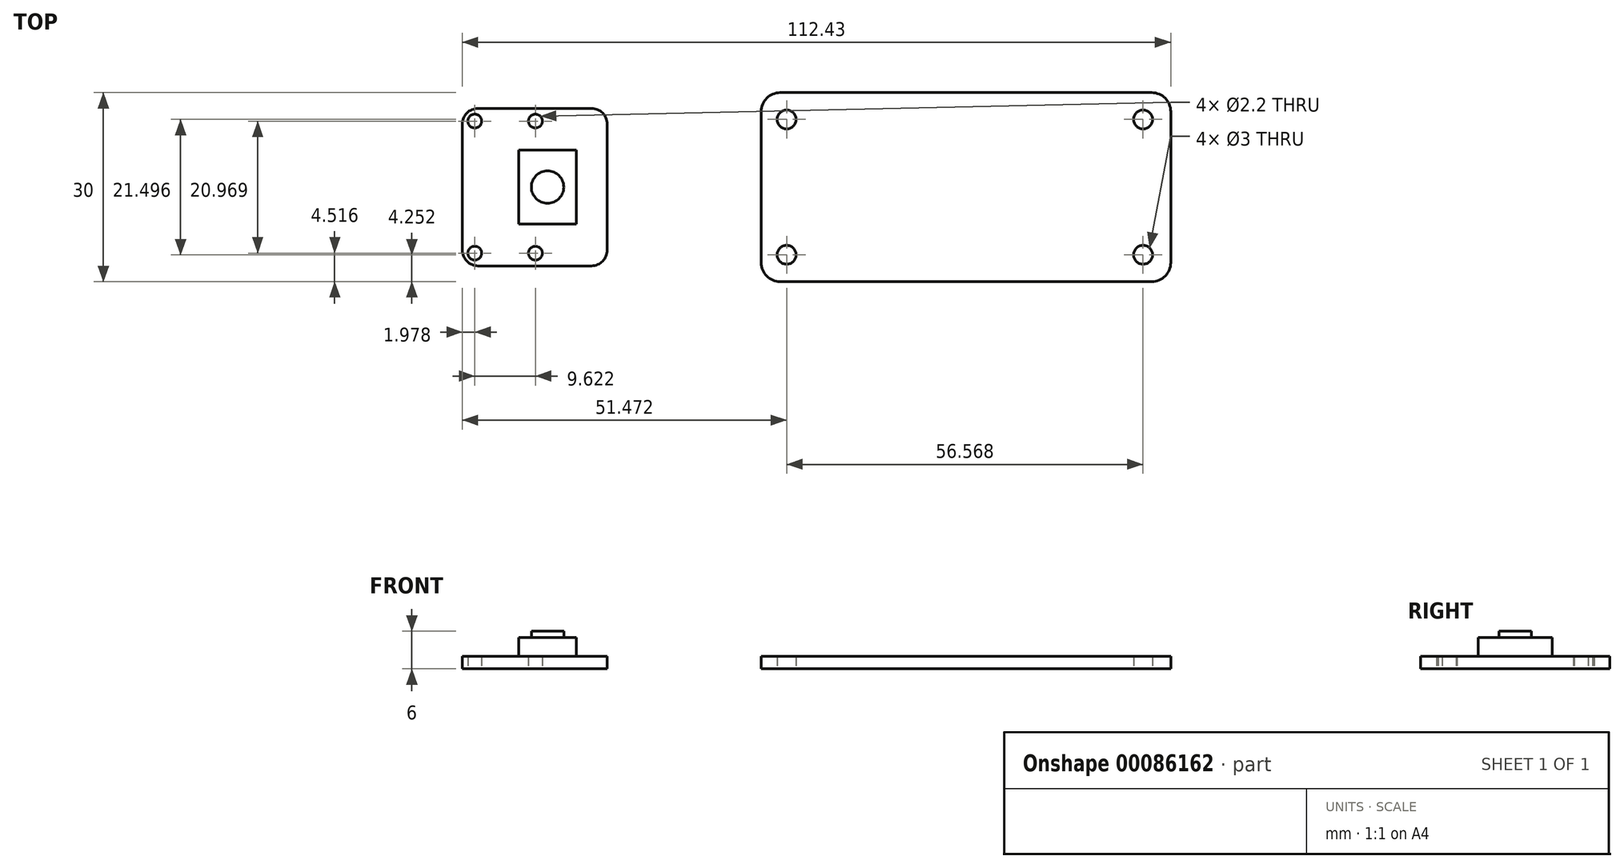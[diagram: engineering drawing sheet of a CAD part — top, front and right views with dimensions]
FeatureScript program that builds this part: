
annotation { "Feature Type Name" : "Feature", "Feature Type Description" : "" }
export const myFeature = defineFeature(function(context is Context, id is Id, definition is map)
    precondition{}
    {
        {
            var Q0;
            Q0=qCreatedBy(makeId("Top.planeOp"),FACE);
            var sketch = newSketch(context, id + "F0", { "sketchPlane" : qUnion([Q0])});
            skLineSegment(sketch, "E0.bottom", {"start": v(-29.5, 15) * mm, "end": v(29.5, 15) * mm});
            skLineSegment(sketch, "E0.top", {"start": v(-29.5, -15) * mm, "end": v(29.5, -15) * mm});
            skLineSegment(sketch, "E0.left", {"start": v(-32.5, 12) * mm, "end": v(-32.5, -12) * mm});
            skLineSegment(sketch, "E0.right", {"start": v(32.5, 12) * mm, "end": v(32.5, -12) * mm});
            skPoint(sketch, "E0.middle", {"position": v(0, 0) * mm});
            skLineSegment(sketch, "E1", {"start": v(-28.46, 35.85) * mm, "end": v(-28.46, -30.94) * mm, "construction": true});
            skLineSegment(sketch, "E2", {"start": v(28.1, 33.55) * mm, "end": v(28.1, -25.56) * mm, "construction": true});
            skLineSegment(sketch, "E3", {"start": v(-45.78, 10.75) * mm, "end": v(56.54, 10.75) * mm, "construction": true});
            skLineSegment(sketch, "E4", {"start": v(-43.57, -10.75) * mm, "end": v(50.84, -10.75) * mm, "construction": true});
            skCircle(sketch, "E5", {"center": v(-28.46, 10.75) * mm, "radius": 1.5 * mm});
            skCircle(sketch, "E6", {"center": v(28.1, 10.75) * mm, "radius": 1.5 * mm});
            skCircle(sketch, "E7", {"center": v(-28.46, -10.75) * mm, "radius": 1.5 * mm});
            skCircle(sketch, "E8", {"center": v(28.1, -10.75) * mm, "radius": 1.5 * mm});
            skPoint(sketch, "E9.visualSharp", {"position": v(-32.5, 15) * mm});
            skArc(sketch, "E9.filletArc", {"start": v(-29.5, 15) * mm, "mid": v(-31.62, 14.12) * mm, "end": v(-32.5, 12) * mm});
            skPoint(sketch, "E10.visualSharp", {"position": v(32.5, 15) * mm});
            skArc(sketch, "E10.filletArc", {"start": v(32.5, 12) * mm, "mid": v(31.62, 14.12) * mm, "end": v(29.5, 15) * mm});
            skPoint(sketch, "E11.visualSharp", {"position": v(32.5, -15) * mm});
            skArc(sketch, "E11.filletArc", {"start": v(29.5, -15) * mm, "mid": v(31.62, -14.12) * mm, "end": v(32.5, -12) * mm});
            skPoint(sketch, "E12.visualSharp", {"position": v(-32.5, -15) * mm});
            skArc(sketch, "E12.filletArc", {"start": v(-32.5, -12) * mm, "mid": v(-31.62, -14.12) * mm, "end": v(-29.5, -15) * mm});
            skSolve(sketch);
        }
        {
            var Q0;
            Q0=makeQuery(id+"F0.imprint","IMPRINT",FACE,{"disambiguationData":[TD([[makeQuery(id+"F0.imprint","IMPRINT",EDGE,{"derivedFrom":sQuery(id+"F0.wireOp",EDGE,"E0.bottom")}),-1.0]])]});
            extrude(context, id + "F1", {"entities" : qUnion([Q0]), "depth" : 2 * mm});
        }
        {
            var Q0;
            Q0=qCreatedBy(makeId("Top.planeOp"),FACE);
            var sketch = newSketch(context, id + "F2", { "sketchPlane" : qUnion([Q0])});
            skLineSegment(sketch, "E13.bottom", {"start": v(-77.43, 12.5) * mm, "end": v(-59.43, 12.5) * mm});
            skLineSegment(sketch, "E13.top", {"start": v(-77.43, -12.5) * mm, "end": v(-59.43, -12.5) * mm});
            skLineSegment(sketch, "E13.left", {"start": v(-79.93, 10) * mm, "end": v(-79.93, -10) * mm});
            skLineSegment(sketch, "E13.right", {"start": v(-56.93, 10) * mm, "end": v(-56.93, -10) * mm});
            skPoint(sketch, "E13.middle", {"position": v(-68.43, 0) * mm});
            skCircle(sketch, "E14", {"center": v(-77.95, 10.48) * mm, "radius": 1.1 * mm});
            skCircle(sketch, "E15", {"center": v(-68.33, 10.48) * mm, "radius": 1.1 * mm});
            skPoint(sketch, "E16.visualSharp", {"position": v(-79.93, 12.5) * mm});
            skArc(sketch, "E16.filletArc", {"start": v(-77.43, 12.5) * mm, "mid": v(-79.2, 11.77) * mm, "end": v(-79.93, 10) * mm});
            skPoint(sketch, "E17.visualSharp", {"position": v(-56.93, 12.5) * mm});
            skArc(sketch, "E17.filletArc", {"start": v(-56.93, 10) * mm, "mid": v(-57.66, 11.77) * mm, "end": v(-59.43, 12.5) * mm});
            skPoint(sketch, "E18.visualSharp", {"position": v(-56.93, -12.5) * mm});
            skArc(sketch, "E18.filletArc", {"start": v(-59.43, -12.5) * mm, "mid": v(-57.66, -11.77) * mm, "end": v(-56.93, -10) * mm});
            skPoint(sketch, "E19.visualSharp", {"position": v(-79.93, -12.5) * mm});
            skArc(sketch, "E19.filletArc", {"start": v(-79.93, -10) * mm, "mid": v(-79.2, -11.77) * mm, "end": v(-77.43, -12.5) * mm});
            skLineSegment(sketch, "E20", {"start": v(-51.58, 10.48) * mm, "end": v(-85.9, 10.48) * mm, "construction": true});
            skCircle(sketch, "E21.MirrorC", {"center": v(-68.33, -10.48) * mm, "radius": 1.1 * mm});
            skCircle(sketch, "E22.MirrorC", {"center": v(-77.95, -10.48) * mm, "radius": 1.1 * mm});
            skLineSegment(sketch, "E23.bottom", {"start": v(-71, 5.89) * mm, "end": v(-61.8, 5.89) * mm});
            skLineSegment(sketch, "E23.top", {"start": v(-71, -5.89) * mm, "end": v(-61.8, -5.89) * mm});
            skLineSegment(sketch, "E23.left", {"start": v(-71, 5.89) * mm, "end": v(-71, -5.89) * mm});
            skLineSegment(sketch, "E23.right", {"start": v(-61.8, 5.89) * mm, "end": v(-61.8, -5.89) * mm});
            skPoint(sketch, "E23.middle", {"position": v(-66.4, 0) * mm});
            skCircle(sketch, "E24", {"center": v(-66.4, 0) * mm, "radius": 2.57 * mm});
            skSolve(sketch);
        }
        {
            var Q0;
            Q0=makeQuery(id+"F2.imprint","IMPRINT",FACE,{"disambiguationData":[TD([[makeQuery(id+"F2.imprint","IMPRINT",EDGE,{"derivedFrom":sQuery(id+"F2.wireOp",EDGE,"E13.bottom")}),-1.0]])]});
            var Q1;
            Q1=makeQuery(id+"F2.imprint","IMPRINT",FACE,{"disambiguationData":[TD([[makeQuery(id+"F2.imprint","IMPRINT",EDGE,{"derivedFrom":sQuery(id+"F2.wireOp",EDGE,"E23.bottom")}),-1.0]])]});
            var Q2;
            Q2=makeQuery(id+"F2.imprint","IMPRINT",FACE,{"disambiguationData":[TD([[makeQuery(id+"F2.imprint","IMPRINT",EDGE,{"derivedFrom":sQuery(id+"F2.wireOp",EDGE,"E24")}),1.0]])]});
            extrude(context, id + "F3", {"entities" : qUnion([Q0, Q1, Q2]), "depth" : 2 * mm});
        }
        {
            var Q0;
            Q0=makeQuery(id+"F2.imprint","IMPRINT",FACE,{"disambiguationData":[TD([[makeQuery(id+"F2.imprint","IMPRINT",EDGE,{"derivedFrom":sQuery(id+"F2.wireOp",EDGE,"E23.bottom")}),-1.0]])]});
            var Q1;
            Q1=makeQuery(id+"F2.imprint","IMPRINT",FACE,{"disambiguationData":[TD([[makeQuery(id+"F2.imprint","IMPRINT",EDGE,{"derivedFrom":sQuery(id+"F2.wireOp",EDGE,"E24")}),1.0]])]});
            extrude(context, id + "F4", {"entities" : qUnion([Q0, Q1]), "operationType" : NewBodyOperationType.ADD, "depth" : 5 * mm});
        }
        {
            var Q0;
            Q0=makeQuery(id+"F2.imprint","IMPRINT",FACE,{"disambiguationData":[TD([[makeQuery(id+"F2.imprint","IMPRINT",EDGE,{"derivedFrom":sQuery(id+"F2.wireOp",EDGE,"E24")}),1.0]])]});
            extrude(context, id + "F5", {"entities" : qUnion([Q0]), "operationType" : NewBodyOperationType.ADD, "depth" : 6 * mm});
        }
    });
